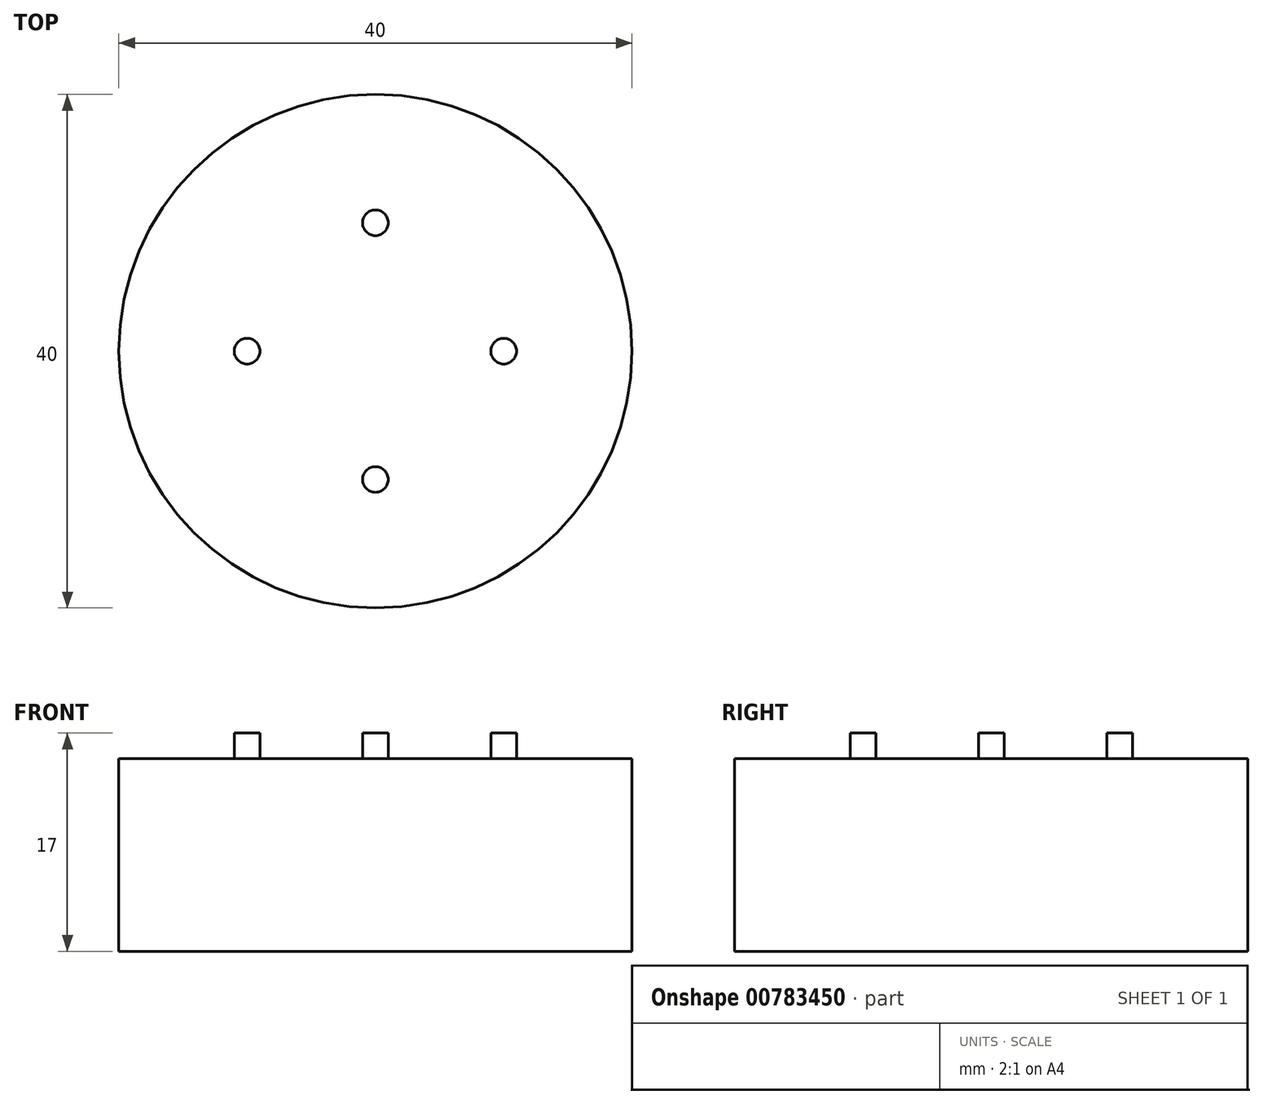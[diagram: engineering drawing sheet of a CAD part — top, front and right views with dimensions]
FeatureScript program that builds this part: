
annotation { "Feature Type Name" : "Feature", "Feature Type Description" : "" }
export const myFeature = defineFeature(function(context is Context, id is Id, definition is map)
    precondition{}
    {
        {
            var Q0;
            Q0=qCreatedBy(makeId("Top.planeOp"),FACE);
            var sketch = newSketch(context, id + "F0", { "sketchPlane" : qUnion([Q0])});
            skCircle(sketch, "E0", {"center": v(0, 0) * mm, "radius": 20 * mm});
            skSolve(sketch);
        }
        {
            var Q0;
            Q0=makeQuery(id+"F0.imprint","IMPRINT",FACE,{"disambiguationData":[TD([[makeQuery(id+"F0.imprint","IMPRINT",EDGE,{"derivedFrom":sQuery(id+"F0.wireOp",EDGE,"E0")}),1.0]])]});
            extrude(context, id + "F1", {"entities" : qUnion([Q0]), "depth" : 15 * mm, "offsetDistance" : 25 * mm});
        }
        {
            var Q0;
            Q0=makeQuery(id+"F1.opExtrude","CAP_FACE",FACE,{"disambiguationData":[OSD([sQuery(id+"F0.wireOp",EDGE,"E0")])],"isStart":false});
            var sketch = newSketch(context, id + "F2", { "sketchPlane" : qUnion([Q0])});
            skLineSegment(sketch, "E1", {"start": v(0, 15) * mm, "end": v(0, -15) * mm, "construction": true});
            skLineSegment(sketch, "E2", {"start": v(15, 0) * mm, "end": v(-15, 0) * mm, "construction": true});
            skCircle(sketch, "E3", {"center": v(0, 0) * mm, "radius": 10 * mm, "construction": true});
            skCircle(sketch, "E4", {"center": v(0, -10) * mm, "radius": 1 * mm});
            skCircle(sketch, "E5", {"center": v(0, 10) * mm, "radius": 1 * mm});
            skCircle(sketch, "E6", {"center": v(10, 0) * mm, "radius": 1 * mm});
            skCircle(sketch, "E7", {"center": v(-10, 0) * mm, "radius": 1 * mm});
            skSolve(sketch);
        }
        {
            var Q0;
            Q0=makeQuery(id+"F2.imprint","IMPRINT",FACE,{"disambiguationData":[TD([[makeQuery(id+"F2.imprint","IMPRINT",EDGE,{"derivedFrom":sQuery(id+"F2.wireOp",EDGE,"E5")}),1.0]])]});
            var Q1;
            Q1=makeQuery(id+"F2.imprint","IMPRINT",FACE,{"disambiguationData":[TD([[makeQuery(id+"F2.imprint","IMPRINT",EDGE,{"derivedFrom":sQuery(id+"F2.wireOp",EDGE,"E6")}),1.0]])]});
            var Q2;
            Q2=makeQuery(id+"F2.imprint","IMPRINT",FACE,{"disambiguationData":[TD([[makeQuery(id+"F2.imprint","IMPRINT",EDGE,{"derivedFrom":sQuery(id+"F2.wireOp",EDGE,"E4")}),1.0]])]});
            var Q3;
            Q3=makeQuery(id+"F2.imprint","IMPRINT",FACE,{"disambiguationData":[TD([[makeQuery(id+"F2.imprint","IMPRINT",EDGE,{"derivedFrom":sQuery(id+"F2.wireOp",EDGE,"E7")}),1.0]])]});
            extrude(context, id + "F3", {"entities" : qUnion([Q0, Q1, Q2, Q3]), "operationType" : NewBodyOperationType.ADD, "depth" : 2 * mm, "offsetDistance" : 25 * mm});
        }
    });
